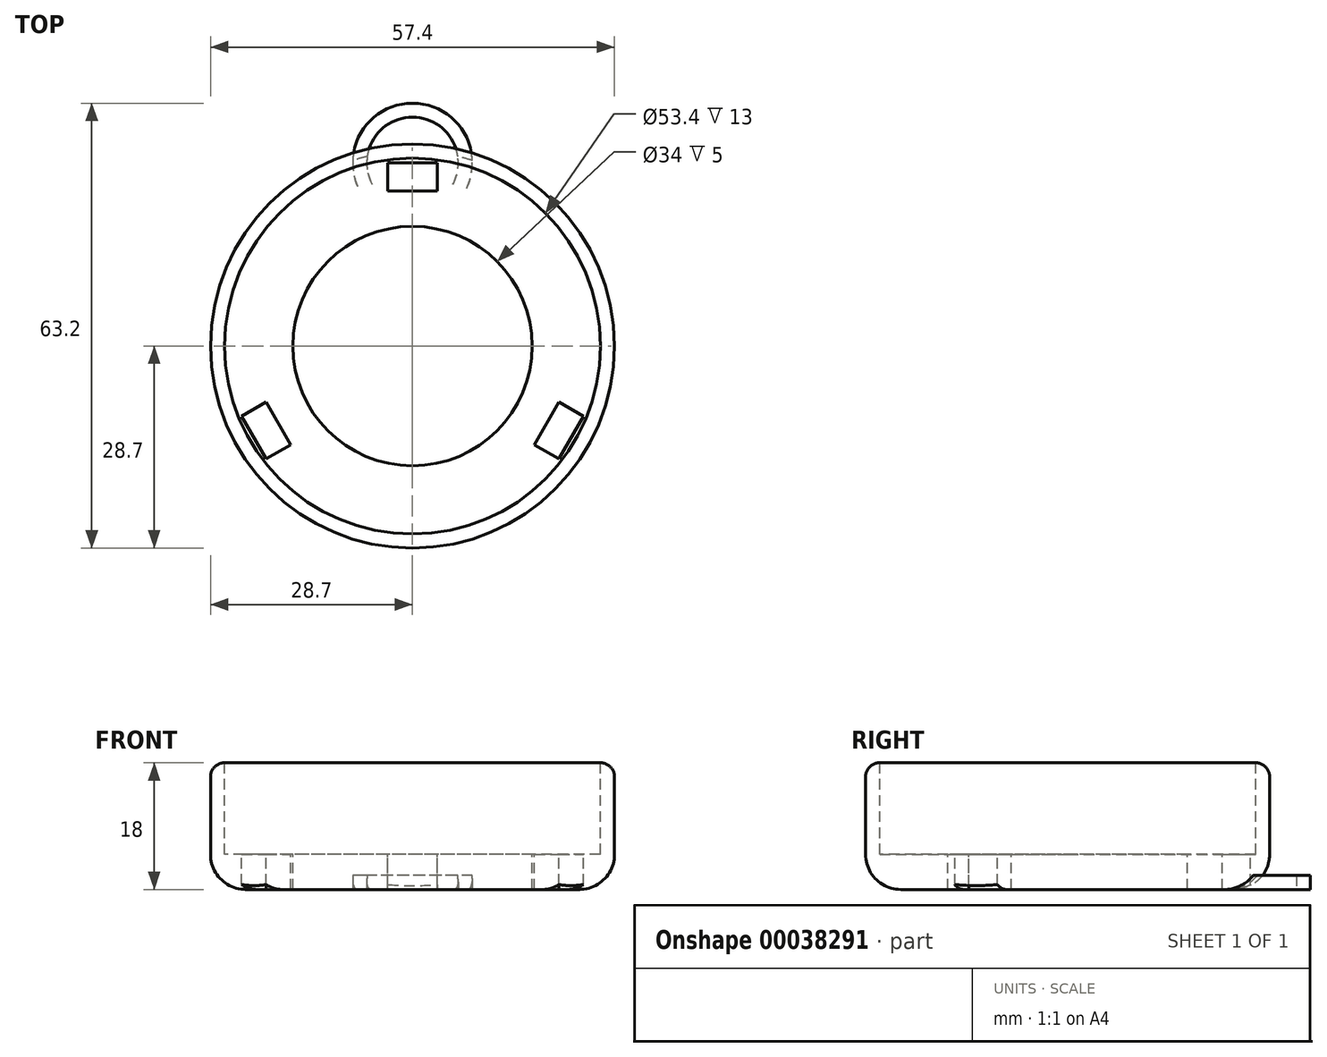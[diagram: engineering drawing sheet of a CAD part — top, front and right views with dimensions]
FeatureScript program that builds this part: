
annotation { "Feature Type Name" : "Feature", "Feature Type Description" : "" }
export const myFeature = defineFeature(function(context is Context, id is Id, definition is map)
    precondition{}
    {
        {
            var Q0;
            Q0=qCreatedBy(makeId("Top.planeOp"),FACE);
            var sketch = newSketch(context, id + "F0", { "sketchPlane" : qUnion([Q0])});
            skCircle(sketch, "E0", {"center": v(0, 0) * mm, "radius": 26.7 * mm});
            skCircle(sketch, "E1", {"center": v(0, 0) * mm, "radius": 28.7 * mm});
            skLineSegment(sketch, "E2", {"start": v(26.7, 0) * mm, "end": v(28.7, 0) * mm, "construction": true});
            skSolve(sketch);
        }
        {
            var Q0;
            Q0 = qSketchRegion(id + "F0", true);
            var Q1;
            Q1=makeQuery(id+"F0.imprint","IMPRINT",FACE,{"disambiguationData":[TD([[makeQuery(id+"F0.imprint","IMPRINT",EDGE,{"derivedFrom":sQuery(id+"F0.wireOp",EDGE,"E0")}),1.0]])]});
            extrude(context, id + "F1", {"entities" : qUnion([Q0, Q1]), "depth" : 18 * mm});
        }
        {
            var Q0;
            Q0=makeQuery(id+"F1.opExtrude","CAP_FACE",FACE,{"disambiguationData":[OSD([sQuery(id+"F0.wireOp",EDGE,"E1")])],"isStart":false});
            var sketch = newSketch(context, id + "F2", { "sketchPlane" : qUnion([Q0])});
            skCircle(sketch, "E3.0", {"center": v(0, 0) * mm, "radius": 26.7 * mm});
            skSolve(sketch);
        }
        {
            var Q0;
            Q0 = qSketchRegion(id + "F2", true);
            extrude(context, id + "F3", {"entities" : qUnion([Q0]), "operationType" : NewBodyOperationType.REMOVE, "oppositeDirection" : true, "depth" : 13 * mm});
        }
        {
            var Q0;
            Q0=makeQuery(id+"F3.boolean.opBoolean","COPY",FACE,{"derivedFrom":makeQuery(id+"F3.opExtrude","CAP_FACE",FACE,{"disambiguationData":[OSD([sQuery(id+"F2.wireOp",EDGE,"E3.0")])],"isStart":false})});
            var sketch = newSketch(context, id + "F4", { "sketchPlane" : qUnion([Q0])});
            skCircle(sketch, "E4", {"center": v(0, 0) * mm, "radius": 17 * mm});
            skLineSegment(sketch, "E5", {"start": v(0, 0) * mm, "end": v(0, 24) * mm, "construction": true});
            skLineSegment(sketch, "E6.rect.bottom", {"start": v(3.5, 22) * mm, "end": v(-3.5, 22) * mm});
            skLineSegment(sketch, "E6.rect.top", {"start": v(3.5, 26) * mm, "end": v(-3.5, 26) * mm});
            skLineSegment(sketch, "E6.rect.left", {"start": v(3.5, 22) * mm, "end": v(3.5, 26) * mm});
            skLineSegment(sketch, "E6.rect.right", {"start": v(-3.5, 22) * mm, "end": v(-3.5, 26) * mm});
            skPoint(sketch, "E6.rect.middle", {"position": v(0, 24) * mm});
            skLineSegment(sketch, "E7.1.0", {"start": v(-24.27, -9.97) * mm, "end": v(-20.77, -16.03) * mm});
            skLineSegment(sketch, "E7.1.1", {"start": v(-17.3, -14.03) * mm, "end": v(-20.77, -16.03) * mm});
            skLineSegment(sketch, "E7.1.2", {"start": v(-20.8, -7.97) * mm, "end": v(-17.3, -14.03) * mm});
            skLineSegment(sketch, "E7.1.3", {"start": v(-20.8, -7.97) * mm, "end": v(-24.27, -9.97) * mm});
            skLineSegment(sketch, "E7.2.0", {"start": v(20.77, -16.03) * mm, "end": v(24.27, -9.97) * mm});
            skLineSegment(sketch, "E7.2.1", {"start": v(20.8, -7.97) * mm, "end": v(24.27, -9.97) * mm});
            skLineSegment(sketch, "E7.2.2", {"start": v(17.3, -14.03) * mm, "end": v(20.8, -7.97) * mm});
            skLineSegment(sketch, "E7.2.3", {"start": v(17.3, -14.03) * mm, "end": v(20.77, -16.03) * mm});
            skSolve(sketch);
        }
        {
            var Q0;
            Q0 = qSketchRegion(id + "F4", true);
            extrude(context, id + "F5", {"entities" : qUnion([Q0]), "operationType" : NewBodyOperationType.REMOVE, "endBound" : BoundingType.THROUGH_ALL, "oppositeDirection" : true, "depth" : 25 * mm});
        }
        {
            var Q0;
            Q0=makeQuery(id+"F1.opExtrude","CAP_EDGE",EDGE,{"disambiguationData":[OSD([sQuery(id+"F0.wireOp",EDGE,"E1")])],"isStart":true});
            fillet(context, id + "F6", {"entities" : qUnion([Q0]), "radius" : 5 * mm, "tangentPropagation" : true, "allowEdgeOverflow" : false});
        }
        {
            var Q0;
            Q0=makeQuery(id+"F1.opExtrude","CAP_EDGE",EDGE,{"disambiguationData":[OSD([sQuery(id+"F0.wireOp",EDGE,"E1")])],"isStart":false});
            fillet(context, id + "F7", {"entities" : qUnion([Q0]), "radius" : 2 * mm, "tangentPropagation" : true, "allowEdgeOverflow" : false});
        }
        {
            var Q0;
            Q0=qCreatedBy(makeId("Top.planeOp"),FACE);
            var sketch = newSketch(context, id + "F8", { "sketchPlane" : qUnion([Q0])});
            skFitSpline(sketch, "E8.0", {"points": [v(-3.5, 26) * mm, v(-1.17, 26) * mm, v(1.17, 26) * mm, v(3.5, 26) * mm], "construction": true});
            skCircle(sketch, "E9", {"center": v(0, 26) * mm, "radius": 8.5 * mm});
            skCircle(sketch, "E10", {"center": v(0, 26) * mm, "radius": 6.5 * mm});
            skLineSegment(sketch, "E11", {"start": v(0, 32.5) * mm, "end": v(0, 34.5) * mm, "construction": true});
            skSolve(sketch);
        }
        {
            var Q0;
            Q0 = qSketchRegion(id + "F8", true);
            extrude(context, id + "F9", {"entities" : qUnion([Q0]), "operationType" : NewBodyOperationType.ADD, "depth" : 2 * mm});
        }
    });
